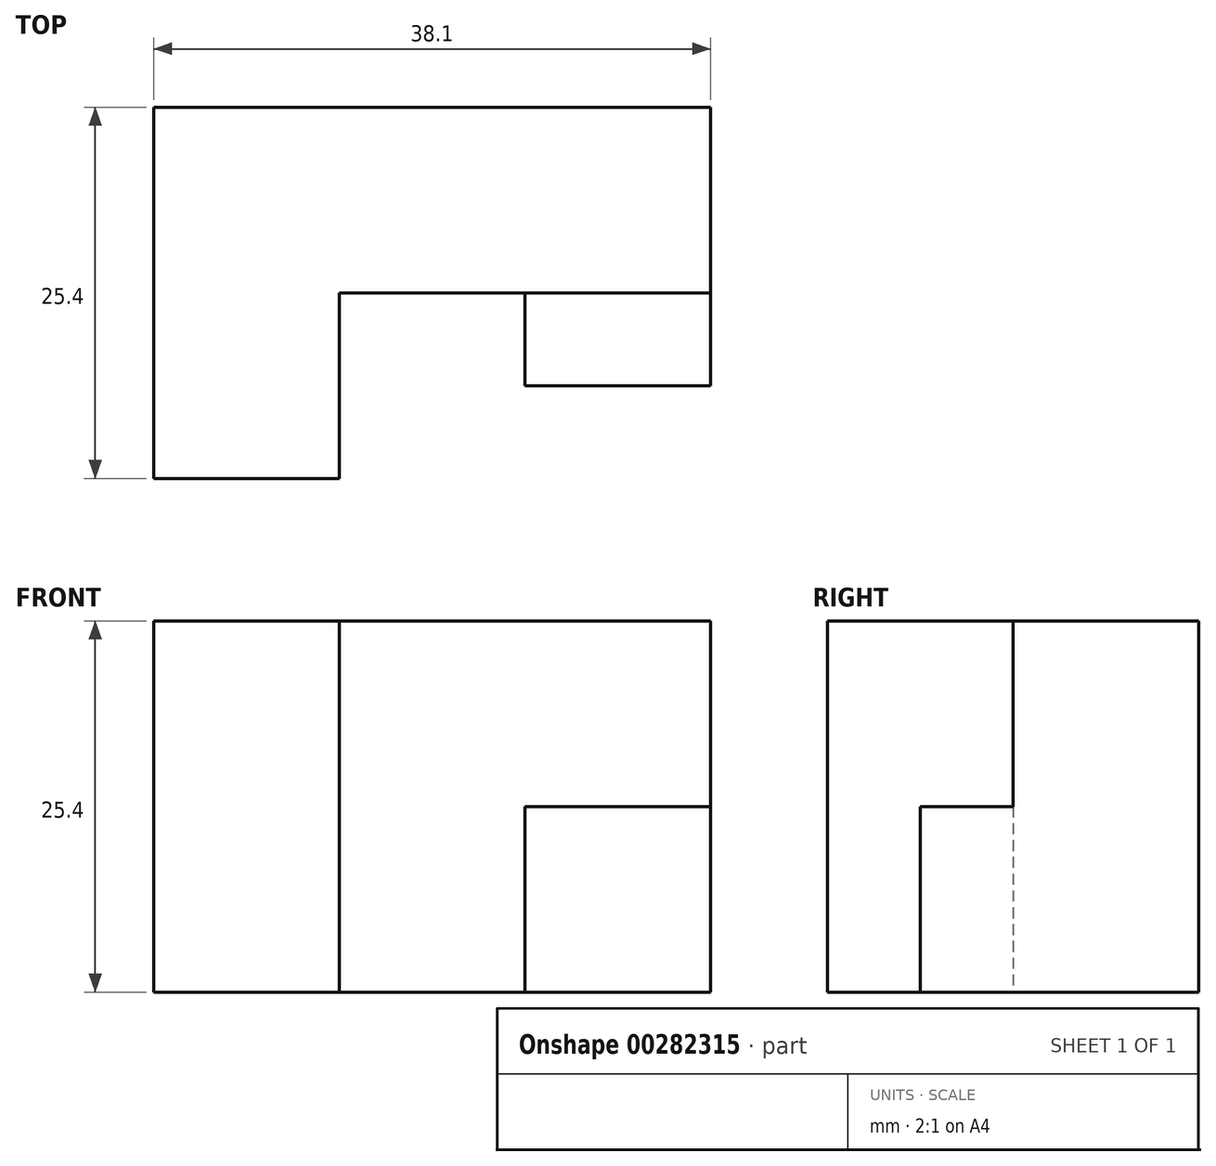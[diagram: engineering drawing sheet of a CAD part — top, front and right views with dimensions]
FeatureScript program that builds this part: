
annotation { "Feature Type Name" : "Feature", "Feature Type Description" : "" }
export const myFeature = defineFeature(function(context is Context, id is Id, definition is map)
    precondition{}
    {
        {
            var Q0;
            Q0=qCreatedBy(makeId("Top.planeOp"),FACE);
            var sketch = newSketch(context, id + "F0", { "sketchPlane" : qUnion([Q0])});
            skLineSegment(sketch, "E0", {"start": v(0, 0) * mm, "end": v(0, 25.4) * mm});
            skLineSegment(sketch, "E1", {"start": v(0, 25.4) * mm, "end": v(38.1, 25.4) * mm});
            skLineSegment(sketch, "E2", {"start": v(38.1, 25.4) * mm, "end": v(38.1, 12.7) * mm});
            skLineSegment(sketch, "E3", {"start": v(38.1, 12.7) * mm, "end": v(12.7, 12.7) * mm});
            skLineSegment(sketch, "E4", {"start": v(12.7, 12.7) * mm, "end": v(12.7, 0) * mm});
            skLineSegment(sketch, "E5", {"start": v(12.7, 0) * mm, "end": v(0, 0) * mm});
            skSolve(sketch);
        }
        {
            var Q0;
            Q0=makeQuery(id+"F0.imprint","IMPRINT",FACE,{"disambiguationData":[TD([[makeQuery(id+"F0.imprint","IMPRINT",EDGE,{"derivedFrom":sQuery(id+"F0.wireOp",EDGE,"E0")}),-1.0]])]});
            extrude(context, id + "F1", {"entities" : qUnion([Q0]), "depth" : 25.4 * mm});
        }
        {
            var Q0;
            Q0=makeQuery(id+"F1.opExtrude","SWEPT_FACE",FACE,{"disambiguationData":[OSD([sQuery(id+"F0.wireOp",EDGE,"E3")])]});
            var sketch = newSketch(context, id + "F2", { "sketchPlane" : qUnion([Q0])});
            skLineSegment(sketch, "E6", {"start": v(38.1, 0) * mm, "end": v(38.1, 12.7) * mm});
            skLineSegment(sketch, "E7", {"start": v(38.1, 12.7) * mm, "end": v(25.4, 12.7) * mm});
            skLineSegment(sketch, "E8", {"start": v(25.4, 12.7) * mm, "end": v(25.4, 0) * mm});
            skLineSegment(sketch, "E9", {"start": v(25.4, 0) * mm, "end": v(38.1, 0) * mm});
            skSolve(sketch);
        }
        {
            var Q0;
            Q0 = qSketchRegion(id + "F2", true);
            extrude(context, id + "F3", {"entities" : qUnion([Q0]), "operationType" : NewBodyOperationType.ADD, "depth" : 6.35 * mm});
        }
    });
